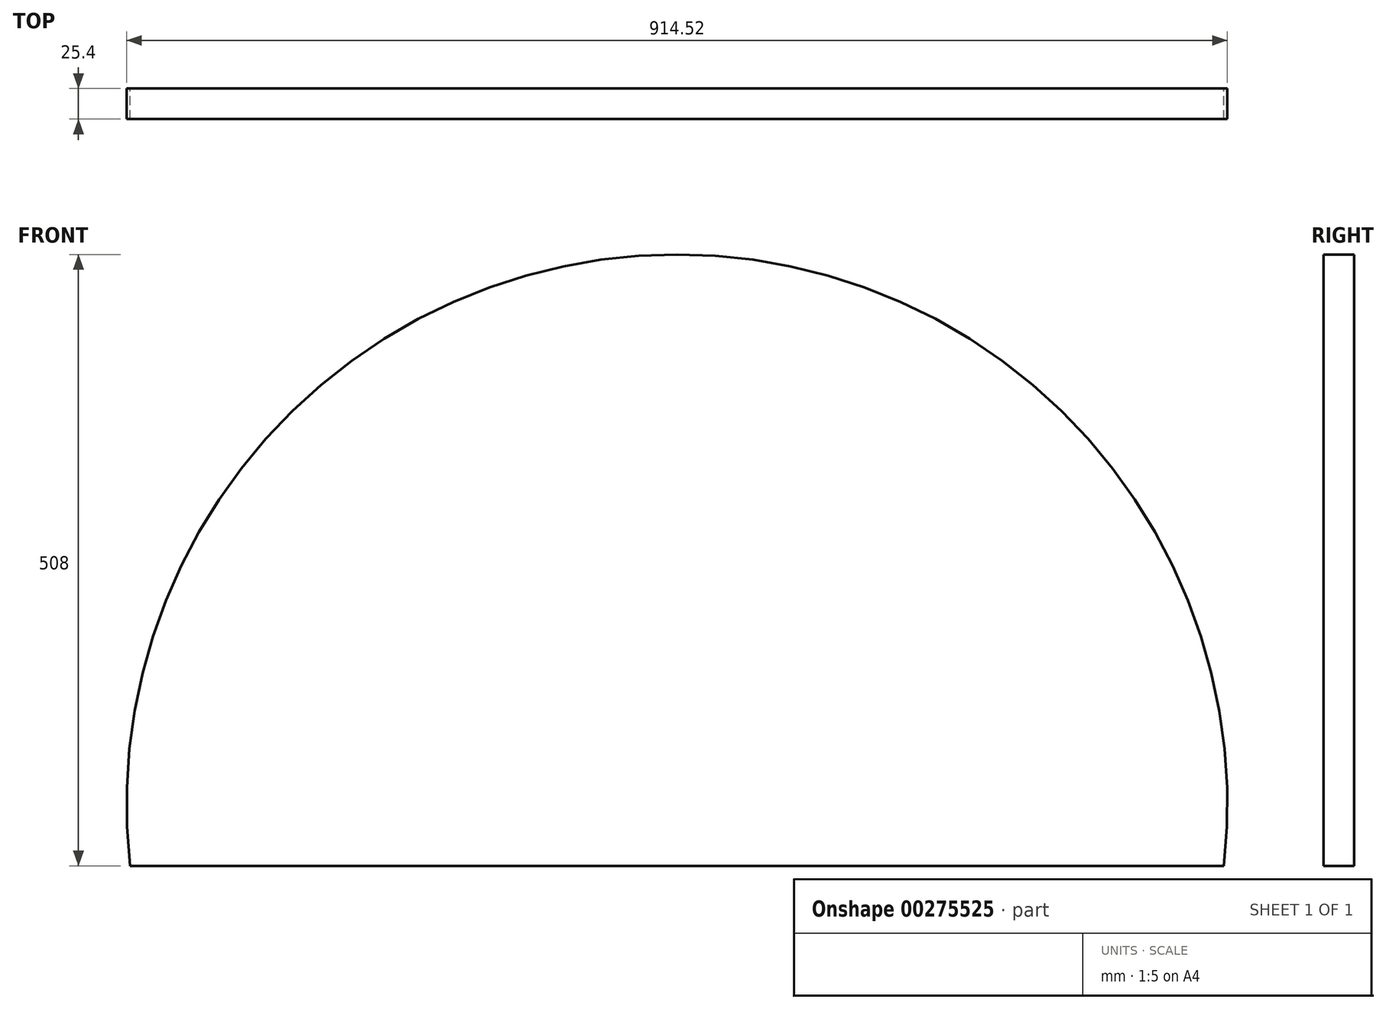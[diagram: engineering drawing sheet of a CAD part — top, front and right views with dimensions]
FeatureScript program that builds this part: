
annotation { "Feature Type Name" : "Feature", "Feature Type Description" : "" }
export const myFeature = defineFeature(function(context is Context, id is Id, definition is map)
    precondition{}
    {
        {
            var Q0;
            Q0=qCreatedBy(makeId("Front.planeOp"),FACE);
            var sketch = newSketch(context, id + "F0", { "sketchPlane" : qUnion([Q0])});
            skLineSegment(sketch, "E0", {"start": v(-452, -263.47) * mm, "end": v(456.87, -263.47) * mm});
            skArc(sketch, "E1", {"start": v(456.87, -263.47) * mm, "mid": v(2.43, 244.53) * mm, "end": v(-452, -263.47) * mm});
            skSolve(sketch);
        }
        {
            var Q0;
            Q0 = qSketchRegion(id + "F0", true);
            extrude(context, id + "F1", {"entities" : qUnion([Q0]), "depth" : 25.4 * mm});
        }
    });
